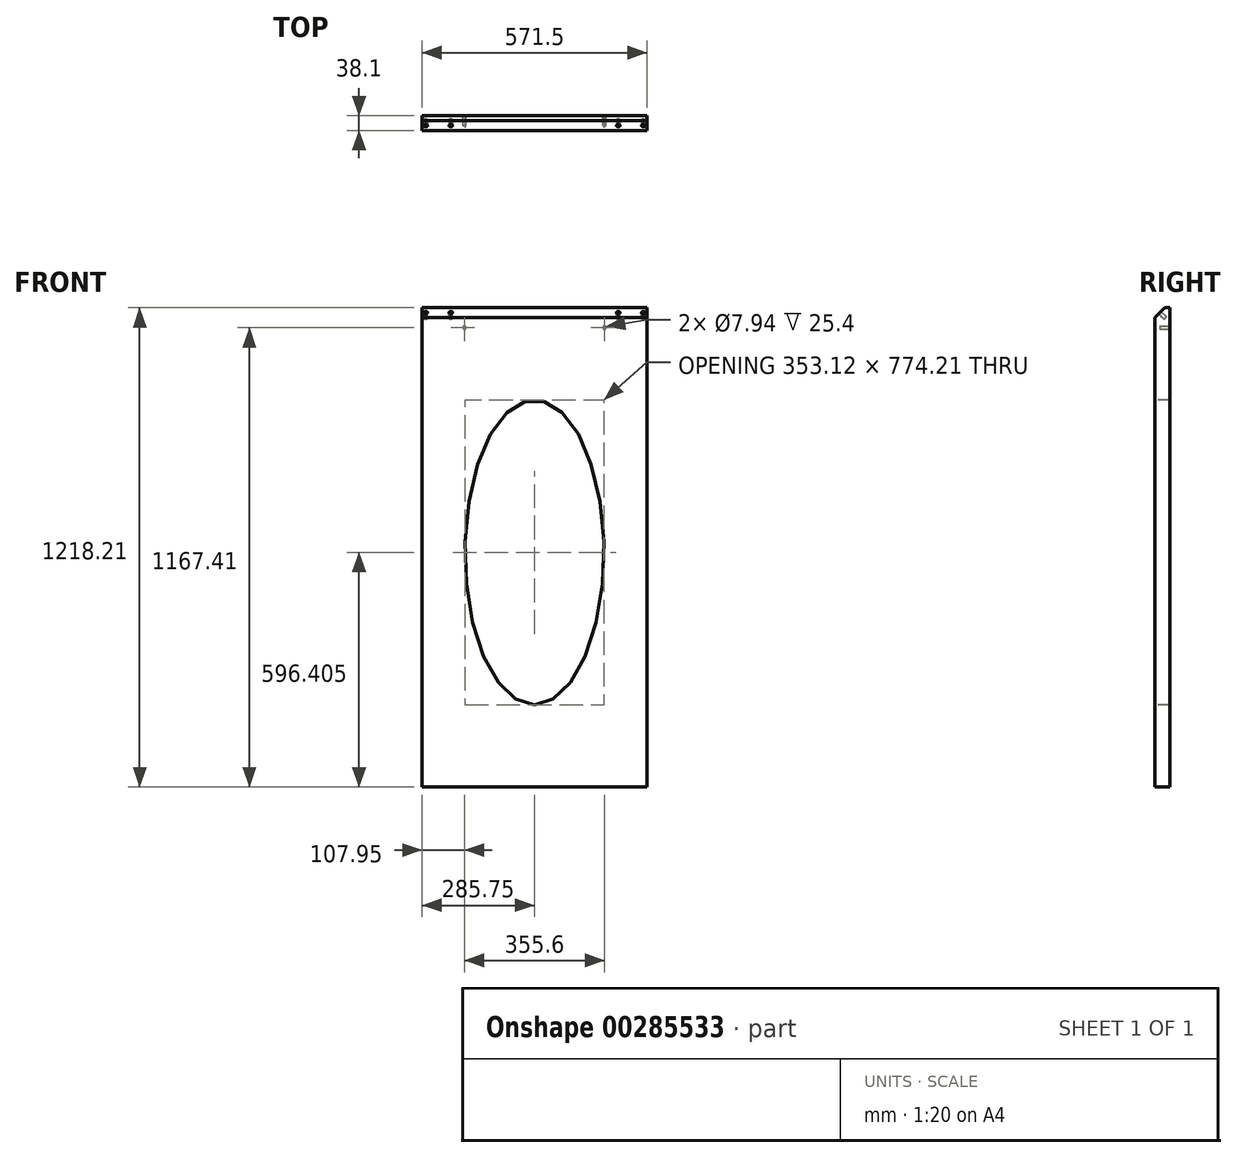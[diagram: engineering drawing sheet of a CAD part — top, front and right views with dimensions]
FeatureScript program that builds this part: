
annotation { "Feature Type Name" : "Feature", "Feature Type Description" : "" }
export const myFeature = defineFeature(function(context is Context, id is Id, definition is map)
    precondition{}
    {
        {
            var Q0;
            Q0=qCreatedBy(makeId("Front.planeOp"),FACE);
            var sketch = newSketch(context, id + "F0", { "sketchPlane" : qUnion([Q0])});
            skLineSegment(sketch, "E0", {"start": v(0, 0) * mm, "end": v(0, 1218.2) * mm});
            skLineSegment(sketch, "E1.0", {"start": v(571.5, 0) * mm, "end": v(571.5, 1218.2) * mm});
            skLineSegment(sketch, "E2", {"start": v(0, 1218.2) * mm, "end": v(571.5, 1218.2) * mm});
            skLineSegment(sketch, "E3", {"start": v(0, 0) * mm, "end": v(571.5, 0) * mm});
            skSolve(sketch);
        }
        {
            var Q0;
            Q0 = qSketchRegion(id + "F0", true);
            extrude(context, id + "F1", {"entities" : qUnion([Q0]), "depth" : 38.1 * mm});
        }
        {
            var Q0;
            Q0=makeQuery(id+"F1.opExtrude","CAP_EDGE",EDGE,{"disambiguationData":[OSD([sQuery(id+"F0.wireOp",EDGE,"E2")])],"isStart":false});
            chamfer(context, id + "F2", {"entities" : qUnion([Q0]), "chamferType" : ChamferType.OFFSET_ANGLE, "width" : 25.4 * mm, "oppositeDirection" : false, "angle" : 45 * degree, "tangentPropagation" : true});
        }
        {
            var Q0;
            Q0=makeQuery(id+"F1.opExtrude","CAP_FACE",FACE,{"disambiguationData":[OSD([sQuery(id+"F0.wireOp",EDGE,"E0"),sQuery(id+"F0.wireOp",EDGE,"E1.0"),sQuery(id+"F0.wireOp",EDGE,"E2"),sQuery(id+"F0.wireOp",EDGE,"E3")])],"isStart":false});
            var sketch = newSketch(context, id + "F3", { "sketchPlane" : qUnion([Q0])});
            skPoint(sketch, "E4.endSnap0", {"position": v(285.75, 1192.8) * mm});
            skEllipse(sketch, "E5", {"center": v(285.75, 596.4) * mm, "majorRadius": 387.1 * mm, "minorRadius": 176.56 * mm, "majorAxis": v(0, -1)});
            skSolve(sketch);
        }
        {
            var Q0;
            Q0=makeQuery(id+"F3.imprint","IMPRINT",FACE,{"disambiguationData":[TD([[makeQuery(id+"F3.imprint","IMPRINT",EDGE,{"derivedFrom":sQuery(id+"F3.wireOp",EDGE,"E5")}),1.0]])]});
            extrude(context, id + "F4", {"entities" : qUnion([Q0]), "operationType" : NewBodyOperationType.REMOVE, "oppositeDirection" : true, "depth" : 38.1 * mm});
        }
        {
            var Q0;
            Q0=makeQuery(id+"F2.opChamfer","BLEND_FACE",FACE,{"disambiguationData":[OSD([sQuery(id+"F0.wireOp",EDGE,"E2")])]});
            var sketch = newSketch(context, id + "F5", { "sketchPlane" : qUnion([Q0])});
            skLineSegment(sketch, "E6", {"start": v(285.75, 816.5) * mm, "end": v(285.75, 867.53) * mm});
            skLineSegment(sketch, "E7", {"start": v(530.22, 834.46) * mm, "end": v(498.48, 834.46) * mm});
            skLineSegment(sketch, "E8", {"start": v(498.48, 834.46) * mm, "end": v(561.98, 834.46) * mm});
            skPoint(sketch, "E9", {"position": v(498.48, 834.46) * mm});
            skPoint(sketch, "E10", {"position": v(561.98, 834.46) * mm});
            skPoint(sketch, "E11.MirrorP", {"position": v(73.03, 834.46) * mm});
            skPoint(sketch, "E12.MirrorP", {"position": v(9.53, 834.46) * mm});
            skCircle(sketch, "E13", {"center": v(9.53, 834.46) * mm, "radius": 4.36 * mm});
            skCircle(sketch, "E14", {"center": v(73.03, 834.46) * mm, "radius": 4.36 * mm});
            skCircle(sketch, "E15", {"center": v(498.48, 834.46) * mm, "radius": 4.36 * mm});
            skCircle(sketch, "E16", {"center": v(561.98, 834.46) * mm, "radius": 4.36 * mm});
            skLineSegment(sketch, "E17", {"start": v(9.53, 834.46) * mm, "end": v(73.03, 834.46) * mm});
            skSolve(sketch);
        }
        {
            var Q0;
            Q0=makeQuery(id+"F5.imprint","IMPRINT",FACE,{"disambiguationData":[TD([[makeQuery(id+"F5.imprint","IMPRINT",EDGE,{"derivedFrom":sQuery(id+"F5.wireOp",EDGE,"E13")}),1.0]])]});
            var Q1;
            Q1=makeQuery(id+"F5.imprint","IMPRINT",FACE,{"disambiguationData":[TD([[makeQuery(id+"F5.imprint","IMPRINT",EDGE,{"derivedFrom":sQuery(id+"F5.wireOp",EDGE,"E14")}),1.0]])]});
            var Q2;
            Q2=makeQuery(id+"F5.imprint","IMPRINT",FACE,{"disambiguationData":[TD([[makeQuery(id+"F5.imprint","IMPRINT",EDGE,{"derivedFrom":sQuery(id+"F5.wireOp",EDGE,"E15")}),1.0]])]});
            var Q3;
            Q3=makeQuery(id+"F5.imprint","IMPRINT",FACE,{"disambiguationData":[TD([[makeQuery(id+"F5.imprint","IMPRINT",EDGE,{"derivedFrom":sQuery(id+"F5.wireOp",EDGE,"E16")}),1.0]])]});
            extrude(context, id + "F6", {"entities" : qUnion([Q0, Q1, Q2, Q3]), "operationType" : NewBodyOperationType.REMOVE, "oppositeDirection" : true, "depth" : 19.05 * mm});
        }
        {
            var Q0;
            Q0=makeQuery(id+"F1.opExtrude","CAP_FACE",FACE,{"disambiguationData":[OSD([sQuery(id+"F0.wireOp",EDGE,"E0"),sQuery(id+"F0.wireOp",EDGE,"E1.0"),sQuery(id+"F0.wireOp",EDGE,"E2"),sQuery(id+"F0.wireOp",EDGE,"E3")])],"isStart":true});
            var sketch = newSketch(context, id + "F7", { "sketchPlane" : qUnion([Q0])});
            skCircle(sketch, "E18", {"center": v(-463.55, 1167.4) * mm, "radius": 3.97 * mm});
            skCircle(sketch, "E19", {"center": v(-107.95, 1167.4) * mm, "radius": 3.97 * mm});
            skLineSegment(sketch, "E20", {"start": v(-463.55, 1167.4) * mm, "end": v(-571.5, 1167.4) * mm});
            skLineSegment(sketch, "E21", {"start": v(-571.5, 1218.2) * mm, "end": v(-571.5, 1167.4) * mm});
            skSolve(sketch);
        }
        {
            var Q0;
            Q0 = qSketchRegion(id + "F7", true);
            extrude(context, id + "F8", {"entities" : qUnion([Q0]), "operationType" : NewBodyOperationType.REMOVE, "oppositeDirection" : true, "depth" : 25.4 * mm});
        }
    });
